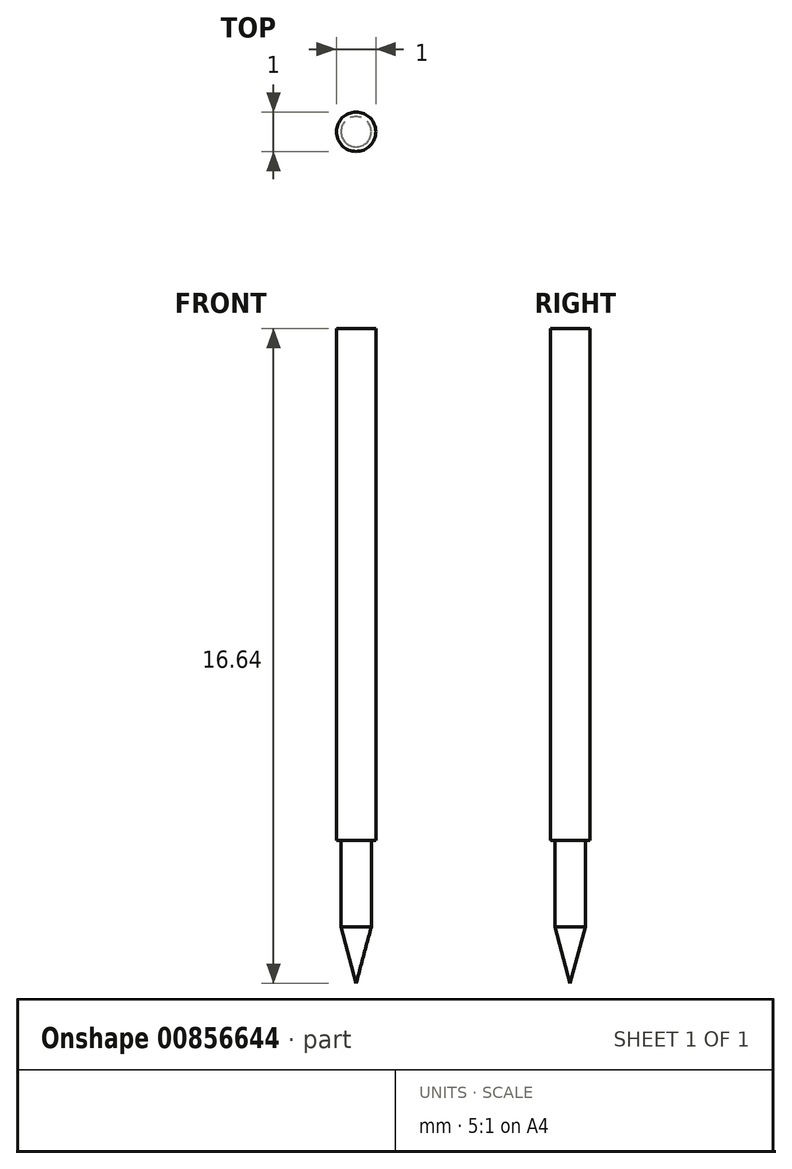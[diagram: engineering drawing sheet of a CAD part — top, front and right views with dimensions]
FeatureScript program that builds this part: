
annotation { "Feature Type Name" : "Feature", "Feature Type Description" : "" }
export const myFeature = defineFeature(function(context is Context, id is Id, definition is map)
    precondition{}
    {
        {
            var Q0;
            Q0=qCreatedBy(makeId("Top.planeOp"),FACE);
            var sketch = newSketch(context, id + "F0", { "sketchPlane" : qUnion([Q0])});
            skCircle(sketch, "E0", {"center": v(0, 0) * mm, "radius": 0.5 * mm});
            skSolve(sketch);
        }
        {
            var Q0;
            Q0=makeQuery(id+"F0.imprint","IMPRINT",FACE,{"disambiguationData":[TD([[makeQuery(id+"F0.imprint","IMPRINT",EDGE,{"derivedFrom":sQuery(id+"F0.wireOp",EDGE,"E0")}),1.0]])]});
            extrude(context, id + "F1", {"entities" : qUnion([Q0]), "depth" : 13 * mm, "offsetDistance" : 25 * mm});
        }
        {
            var Q0;
            Q0=makeQuery(id+"F1.opExtrude","CAP_FACE",FACE,{"disambiguationData":[OSD([sQuery(id+"F0.wireOp",EDGE,"E0")])],"isStart":true});
            var sketch = newSketch(context, id + "F2", { "sketchPlane" : qUnion([Q0])});
            skCircle(sketch, "E1", {"center": v(0, 0) * mm, "radius": 0.39 * mm});
            skSolve(sketch);
        }
        {
            var Q0;
            Q0=makeQuery(id+"F2.imprint","IMPRINT",FACE,{"disambiguationData":[TD([[makeQuery(id+"F2.imprint","IMPRINT",EDGE,{"derivedFrom":sQuery(id+"F2.wireOp",EDGE,"E1")}),1.0]])]});
            extrude(context, id + "F3", {"entities" : qUnion([Q0]), "operationType" : NewBodyOperationType.ADD, "depth" : 2.2 * mm, "offsetDistance" : 25 * mm});
        }
        {
            var Q0;
            Q0=qCreatedBy(makeId("Front.planeOp"),FACE);
            var sketch = newSketch(context, id + "F4", { "sketchPlane" : qUnion([Q0])});
            skLineSegment(sketch, "E2", {"start": v(0, -3.64) * mm, "end": v(-0.39, -2.2) * mm});
            skLineSegment(sketch, "E3.0", {"start": v(0.39, -2.2) * mm, "end": v(-0.39, -2.2) * mm});
            skLineSegment(sketch, "E4", {"start": v(0.39, -2.2) * mm, "end": v(0, -3.64) * mm});
            skLineSegment(sketch, "E5", {"start": v(0, -3.64) * mm, "end": v(0, -2.2) * mm});
            skSolve(sketch);
        }
        {
            var Q0;
            {var subQ0=sQuery(id+"F4.wireOp",EDGE,"E2");Q0=makeQuery(id+"F4.imprint","IMPRINT",FACE,{"disambiguationData":[TD([[makeQuery(id+"F4.imprint","IMPRINT",EDGE,{"derivedFrom":subQ0}),-1.0]])]});}
            var Q1;
            Q1=sQuery(id+"F4.wireOp",EDGE,"E5");
            revolve(context, id + "F5", {"operationType" : NewBodyOperationType.ADD, "surfaceOperationType" : NewSurfaceOperationType.NEW, "entities" : qUnion([Q0]), "axis" : qUnion([Q1]), "revolveType" : RevolveType.FULL});
        }
    });
